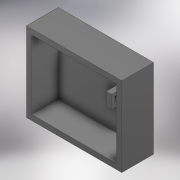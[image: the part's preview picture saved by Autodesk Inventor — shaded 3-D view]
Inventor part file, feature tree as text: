
AUTODESK INVENTOR PART (.ipt)
format: ipt  version: 2020 (Build 240168000, 168)  size: 150,016 bytes
history: native  units: mm
features: extrude x4, sketch x4
ambient origin geometry x8: Origin, YZ Plane, XZ Plane, XY Plane, X Axis, Y Axis, Z Axis, Center Point
bodies: Volumenkörper1 (feature_tree)
feature tree (8):
  extrude  "Extrusion1"  Depth=90.0mm
  extrude  "Extrusion2"  Depth=5.0mm
  extrude  "Extrusion3"  Depth=5.0mm
  extrude  "Extrusion4"  Depth=5.0mm TaperAngle=0.0deg
  sketch  "Skizze1"  dims[d0=75.0mm d1=90.0mm]
  sketch  "Skizze2"  dims[d2=5.0mm d3=5.0mm]
  sketch  "Skizze3"  dims[d4=5.0mm d5=5.0mm]
  sketch  "Skizze4"  dims[d6=25.0mm d7=0.0mm d8=5.0mm d9=0.0mm d10=12.5mm d11=5.0mm d12=26.25mm d13=55.0mm d14=9.5mm d15=0.0mm d16=6.5mm d17=6.5mm d18=3.0mm d19=5.0mm d20=0.0mm]
